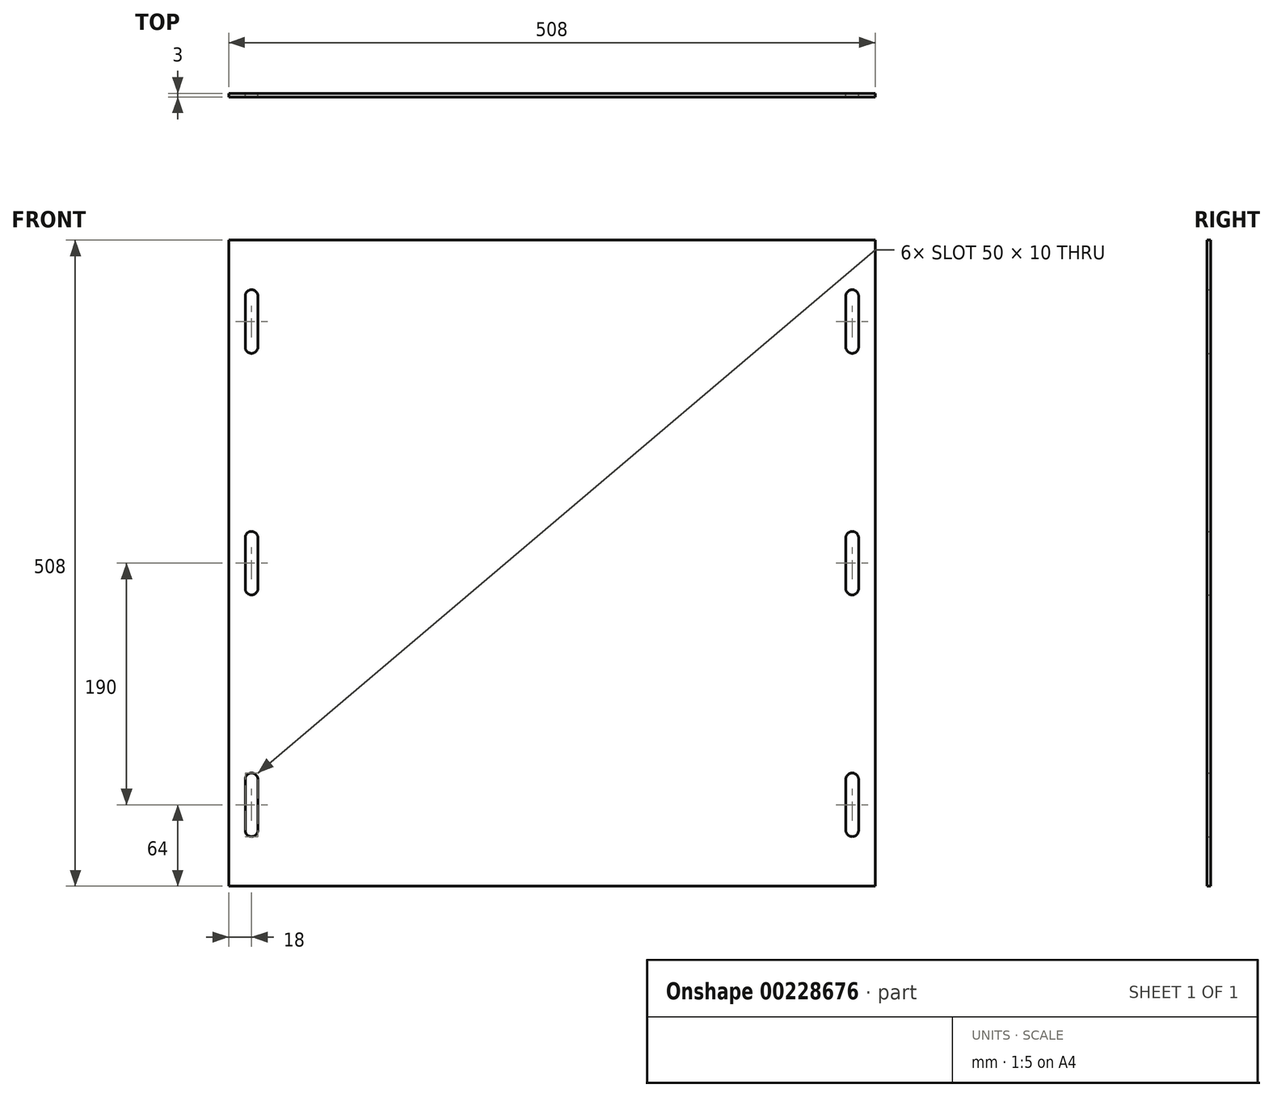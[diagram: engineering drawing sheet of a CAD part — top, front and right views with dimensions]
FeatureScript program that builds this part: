
annotation { "Feature Type Name" : "Feature", "Feature Type Description" : "" }
export const myFeature = defineFeature(function(context is Context, id is Id, definition is map)
    precondition{}
    {
        {
            var Q0;
            Q0=qCreatedBy(makeId("Front.planeOp"),FACE);
            var sketch = newSketch(context, id + "F0", { "sketchPlane" : qUnion([Q0])});
            skLineSegment(sketch, "E0.bottom", {"start": v(0, 0) * mm, "end": v(508, 0) * mm});
            skLineSegment(sketch, "E0.top", {"start": v(0, 508) * mm, "end": v(508, 508) * mm});
            skLineSegment(sketch, "E0.left", {"start": v(0, 0) * mm, "end": v(0, 508) * mm});
            skLineSegment(sketch, "E0.right", {"start": v(508, 0) * mm, "end": v(508, 508) * mm});
            skLineSegment(sketch, "E1", {"start": v(18, 508) * mm, "end": v(18, 0) * mm, "construction": true});
            skLineSegment(sketch, "E2", {"start": v(490, 508) * mm, "end": v(490, 0) * mm, "construction": true});
            skArc(sketch, "E3", {"start": v(23, 464) * mm, "mid": v(18, 469) * mm, "end": v(13, 464) * mm});
            skArc(sketch, "E4", {"start": v(13, 424) * mm, "mid": v(18, 419) * mm, "end": v(23, 424) * mm});
            skArc(sketch, "E5", {"start": v(23, 274) * mm, "mid": v(18, 279) * mm, "end": v(13, 274) * mm});
            skArc(sketch, "E6", {"start": v(13, 234) * mm, "mid": v(18, 229) * mm, "end": v(23, 234) * mm});
            skArc(sketch, "E7", {"start": v(23, 84) * mm, "mid": v(18, 89) * mm, "end": v(13, 84) * mm});
            skArc(sketch, "E8", {"start": v(13, 44) * mm, "mid": v(18, 39) * mm, "end": v(23, 44) * mm});
            skLineSegment(sketch, "E9", {"start": v(13, 464) * mm, "end": v(13, 424) * mm});
            skLineSegment(sketch, "E10", {"start": v(23, 464) * mm, "end": v(23, 424) * mm});
            skLineSegment(sketch, "E11", {"start": v(13, 274) * mm, "end": v(13, 234) * mm});
            skLineSegment(sketch, "E12", {"start": v(23, 274) * mm, "end": v(23, 234) * mm});
            skLineSegment(sketch, "E13", {"start": v(13, 84) * mm, "end": v(13, 44) * mm});
            skLineSegment(sketch, "E14", {"start": v(23, 84) * mm, "end": v(23, 44) * mm});
            skArc(sketch, "E15", {"start": v(495, 464) * mm, "mid": v(490, 469) * mm, "end": v(485, 464) * mm});
            skArc(sketch, "E16", {"start": v(485, 424) * mm, "mid": v(490, 419) * mm, "end": v(495, 424) * mm});
            skArc(sketch, "E17", {"start": v(495, 274) * mm, "mid": v(490, 279) * mm, "end": v(485, 274) * mm});
            skArc(sketch, "E18", {"start": v(485, 234) * mm, "mid": v(490, 229) * mm, "end": v(495, 234) * mm});
            skArc(sketch, "E19", {"start": v(485, 44) * mm, "mid": v(490, 39) * mm, "end": v(495, 44) * mm});
            skArc(sketch, "E20", {"start": v(495, 84) * mm, "mid": v(490, 89) * mm, "end": v(485, 84) * mm});
            skLineSegment(sketch, "E21", {"start": v(485, 464) * mm, "end": v(485, 424) * mm});
            skLineSegment(sketch, "E22", {"start": v(495, 464) * mm, "end": v(495, 424) * mm});
            skLineSegment(sketch, "E23", {"start": v(485, 274) * mm, "end": v(485, 234) * mm});
            skLineSegment(sketch, "E24", {"start": v(495, 274) * mm, "end": v(495, 234) * mm});
            skLineSegment(sketch, "E25", {"start": v(485, 84) * mm, "end": v(485, 44) * mm});
            skLineSegment(sketch, "E26", {"start": v(495, 84) * mm, "end": v(495, 44) * mm});
            skSolve(sketch);
        }
        {
            var Q0;
            Q0=qSketchRegion(id+"F0",true);
            extrude(context, id + "F1", {"entities" : qUnion([Q0]), "depth" : 3 * mm});
        }
    });
